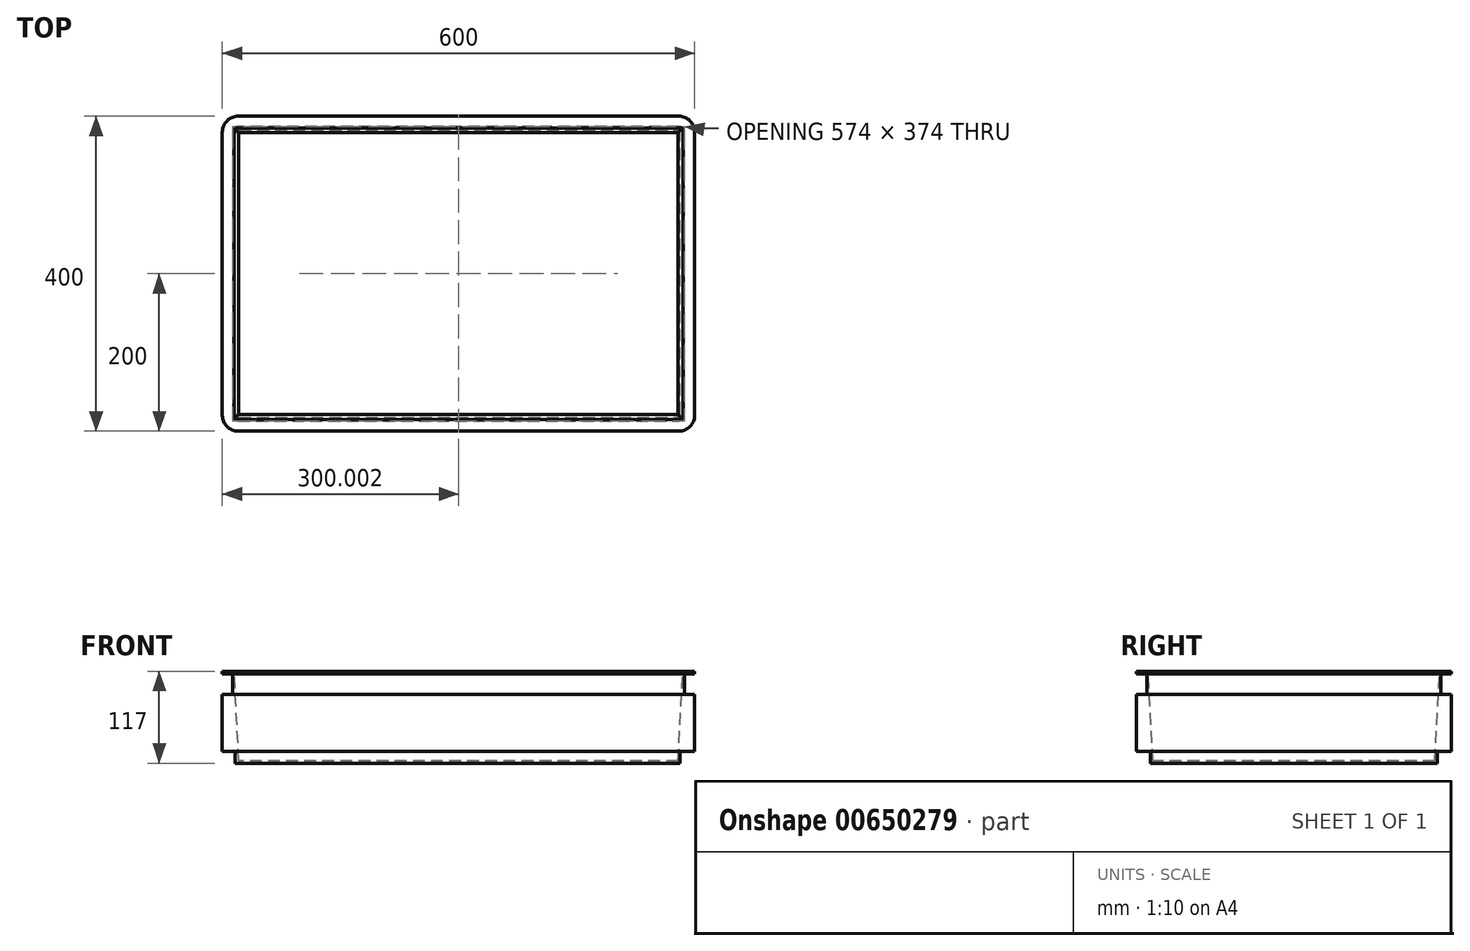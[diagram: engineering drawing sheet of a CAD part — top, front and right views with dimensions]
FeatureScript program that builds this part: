
annotation { "Feature Type Name" : "Feature", "Feature Type Description" : "" }
export const myFeature = defineFeature(function(context is Context, id is Id, definition is map)
    precondition{}
    {
        {
            var Q0;
            Q0=qCreatedBy(makeId("Top.planeOp"),FACE);
            var sketch = newSketch(context, id + "F0", { "sketchPlane" : qUnion([Q0])});
            skLineSegment(sketch, "E0.bottom", {"start": v(-291.39, 200) * mm, "end": v(308.61, 200) * mm});
            skLineSegment(sketch, "E0.top", {"start": v(-291.39, -200) * mm, "end": v(308.61, -200) * mm});
            skLineSegment(sketch, "E0.left", {"start": v(-291.39, 200) * mm, "end": v(-291.39, -200) * mm});
            skLineSegment(sketch, "E0.right", {"start": v(308.61, 200) * mm, "end": v(308.61, -200) * mm});
            skPoint(sketch, "E0.middle", {"position": v(8.61, 0) * mm});
            skSolve(sketch);
        }
        {
            var Q0;
            Q0=makeQuery(id+"F0.imprint","IMPRINT",FACE,{"disambiguationData":[TD([[makeQuery(id+"F0.imprint","IMPRINT",EDGE,{"derivedFrom":sQuery(id+"F0.wireOp",EDGE,"E0.bottom")}),-1.0]])]});
            extrude(context, id + "F1", {"entities" : qUnion([Q0]), "depth" : 117 * mm, "offsetDistance" : 25 * mm});
        }
        {
            var Q0;
            Q0=makeQuery(id+"F1.opExtrude","SWEPT_EDGE",EDGE,{"disambiguationData":[OSD([sQuery(id+"F0.wireOp",EDGE,"E0.top"),sQuery(id+"F0.wireOp",EDGE,"E0.left")])]});
            var Q1;
            Q1=makeQuery(id+"F1.opExtrude","SWEPT_EDGE",EDGE,{"disambiguationData":[OSD([sQuery(id+"F0.wireOp",EDGE,"E0.top"),sQuery(id+"F0.wireOp",EDGE,"E0.right")])]});
            var Q2;
            Q2=makeQuery(id+"F1.opExtrude","SWEPT_EDGE",EDGE,{"disambiguationData":[OSD([sQuery(id+"F0.wireOp",EDGE,"E0.bottom"),sQuery(id+"F0.wireOp",EDGE,"E0.right")])]});
            var Q3;
            Q3=makeQuery(id+"F1.opExtrude","SWEPT_EDGE",EDGE,{"disambiguationData":[OSD([sQuery(id+"F0.wireOp",EDGE,"E0.bottom"),sQuery(id+"F0.wireOp",EDGE,"E0.left")])]});
            fillet(context, id + "F2", {"entities" : qUnion([Q0, Q1, Q2, Q3]), "radius" : 20 * mm, "tangentPropagation" : true, "allowEdgeOverflow" : false});
        }
        {
            var Q0;
            Q0=makeQuery(id+"F1.opExtrude","CAP_FACE",FACE,{"disambiguationData":[OSD([sQuery(id+"F0.wireOp",EDGE,"E0.bottom"),sQuery(id+"F0.wireOp",EDGE,"E0.top"),sQuery(id+"F0.wireOp",EDGE,"E0.left"),sQuery(id+"F0.wireOp",EDGE,"E0.right")])],"isStart":true});
            var sketch = newSketch(context, id + "F3", { "sketchPlane" : qUnion([Q0])});
            skLineSegment(sketch, "E1.bottom", {"start": v(-270.1, 182.5) * mm, "end": v(284.9, 182.5) * mm});
            skLineSegment(sketch, "E1.top", {"start": v(-270.1, -182.5) * mm, "end": v(284.9, -182.5) * mm});
            skLineSegment(sketch, "E1.left", {"start": v(-275.1, 177.5) * mm, "end": v(-275.1, -177.5) * mm});
            skLineSegment(sketch, "E1.right", {"start": v(289.9, 177.5) * mm, "end": v(289.9, -177.5) * mm});
            skPoint(sketch, "E1.middle", {"position": v(7.4, 0) * mm});
            skLineSegment(sketch, "E2.0.0", {"start": v(288.61, 200) * mm, "end": v(-271.39, 200) * mm});
            skArc(sketch, "E2.0.1", {"start": v(-271.39, 200) * mm, "mid": v(-285.53, 194.14) * mm, "end": v(-291.39, 180) * mm});
            skLineSegment(sketch, "E2.0.2", {"start": v(-291.39, 180) * mm, "end": v(-291.39, -180) * mm});
            skArc(sketch, "E2.0.3", {"start": v(-291.39, -180) * mm, "mid": v(-285.53, -194.14) * mm, "end": v(-271.39, -200) * mm});
            skLineSegment(sketch, "E2.0.4", {"start": v(-271.39, -200) * mm, "end": v(288.61, -200) * mm});
            skArc(sketch, "E2.0.5", {"start": v(288.61, -200) * mm, "mid": v(302.75, -194.14) * mm, "end": v(308.61, -180) * mm});
            skLineSegment(sketch, "E2.0.6", {"start": v(308.61, -180) * mm, "end": v(308.61, 180) * mm});
            skArc(sketch, "E2.0.7", {"start": v(308.61, 180) * mm, "mid": v(302.75, 194.14) * mm, "end": v(288.61, 200) * mm});
            skPoint(sketch, "E3.visualSharp", {"position": v(-275.1, 182.5) * mm});
            skArc(sketch, "E3.filletArc", {"start": v(-270.1, 182.5) * mm, "mid": v(-273.63, 181.04) * mm, "end": v(-275.1, 177.5) * mm});
            skPoint(sketch, "E4.visualSharp", {"position": v(289.9, 182.5) * mm});
            skArc(sketch, "E4.filletArc", {"start": v(289.9, 177.5) * mm, "mid": v(288.44, 181.04) * mm, "end": v(284.9, 182.5) * mm});
            skPoint(sketch, "E5.visualSharp", {"position": v(289.9, -182.5) * mm});
            skArc(sketch, "E5.filletArc", {"start": v(284.9, -182.5) * mm, "mid": v(288.44, -181.04) * mm, "end": v(289.9, -177.5) * mm});
            skPoint(sketch, "E6.visualSharp", {"position": v(-275.1, -182.5) * mm});
            skArc(sketch, "E6.filletArc", {"start": v(-275.1, -177.5) * mm, "mid": v(-273.63, -181.04) * mm, "end": v(-270.1, -182.5) * mm});
            skSolve(sketch);
        }
        {
            var Q0;
            Q0=makeQuery(id+"F3.imprint","IMPRINT",FACE,{"disambiguationData":[TD([[makeQuery(id+"F3.imprint","IMPRINT",EDGE,{"derivedFrom":sQuery(id+"F3.wireOp",EDGE,"E1.bottom")}),1.0]])]});
            extrude(context, id + "F4", {"entities" : qUnion([Q0]), "operationType" : NewBodyOperationType.REMOVE, "oppositeDirection" : true, "depth" : 15 * mm, "offsetDistance" : 25 * mm});
        }
        {
            var Q0;
            Q0=makeQuery(id+"F1.opExtrude","CAP_FACE",FACE,{"disambiguationData":[OSD([sQuery(id+"F0.wireOp",EDGE,"E0.bottom"),sQuery(id+"F0.wireOp",EDGE,"E0.top"),sQuery(id+"F0.wireOp",EDGE,"E0.left"),sQuery(id+"F0.wireOp",EDGE,"E0.right")])],"isStart":false});
            cPlane(context, id + "F5", {"entities" : qUnion([Q0]), "cplaneType" : CPlaneType.OFFSET, "offset" : 3.5 * mm, "oppositeDirection" : true, "width" : 150 * mm, "height" : 150 * mm});
        }
        {
            var Q0;
            Q0=qCreatedBy(id+"F5.planeOp",FACE);
            var sketch = newSketch(context, id + "F6", { "sketchPlane" : qUnion([Q0])});
            skLineSegment(sketch, "E7.0.0", {"start": v(-291.39, 180) * mm, "end": v(-291.39, -180) * mm});
            skArc(sketch, "E7.0.1", {"start": v(-291.39, -180) * mm, "mid": v(-285.53, -194.14) * mm, "end": v(-271.39, -200) * mm});
            skLineSegment(sketch, "E7.0.2", {"start": v(-271.39, -200) * mm, "end": v(288.61, -200) * mm});
            skArc(sketch, "E7.0.3", {"start": v(288.61, -200) * mm, "mid": v(302.75, -194.14) * mm, "end": v(308.61, -180) * mm});
            skLineSegment(sketch, "E7.0.4", {"start": v(308.61, -180) * mm, "end": v(308.61, 180) * mm});
            skArc(sketch, "E7.0.5", {"start": v(308.61, 180) * mm, "mid": v(302.75, 194.14) * mm, "end": v(288.61, 200) * mm});
            skLineSegment(sketch, "E7.0.6", {"start": v(288.61, 200) * mm, "end": v(-271.39, 200) * mm});
            skArc(sketch, "E7.0.7", {"start": v(-271.39, 200) * mm, "mid": v(-285.53, 194.14) * mm, "end": v(-291.39, 180) * mm});
            skArc(sketch, "E8.0", {"start": v(-271.39, 187) * mm, "mid": v(-276.34, 184.95) * mm, "end": v(-278.39, 180) * mm});
            skLineSegment(sketch, "E8.1", {"start": v(288.61, 187) * mm, "end": v(-271.39, 187) * mm});
            skLineSegment(sketch, "E8.2", {"start": v(-278.39, 180) * mm, "end": v(-278.39, -180) * mm});
            skArc(sketch, "E8.3", {"start": v(295.61, 180) * mm, "mid": v(293.56, 184.95) * mm, "end": v(288.61, 187) * mm});
            skArc(sketch, "E8.4", {"start": v(-278.39, -180) * mm, "mid": v(-276.34, -184.95) * mm, "end": v(-271.39, -187) * mm});
            skLineSegment(sketch, "E8.5", {"start": v(-271.39, -187) * mm, "end": v(288.61, -187) * mm});
            skArc(sketch, "E8.6", {"start": v(288.61, -187) * mm, "mid": v(293.56, -184.95) * mm, "end": v(295.61, -180) * mm});
            skLineSegment(sketch, "E8.7", {"start": v(295.61, -180) * mm, "end": v(295.61, 180) * mm});
            skSolve(sketch);
        }
        {
            var Q0;
            Q0 = qSketchRegion(id + "F6", true);
            extrude(context, id + "F7", {"entities" : qUnion([Q0]), "operationType" : NewBodyOperationType.REMOVE, "oppositeDirection" : true, "depth" : 26 * mm, "offsetDistance" : 25 * mm});
        }
        {
            var Q0;
            Q0=makeQuery(id+"F1.opExtrude","CAP_FACE",FACE,{"disambiguationData":[OSD([sQuery(id+"F0.wireOp",EDGE,"E0.bottom"),sQuery(id+"F0.wireOp",EDGE,"E0.top"),sQuery(id+"F0.wireOp",EDGE,"E0.left"),sQuery(id+"F0.wireOp",EDGE,"E0.right")])],"isStart":false});
            var sketch = newSketch(context, id + "F8", { "sketchPlane" : qUnion([Q0])});
            skLineSegment(sketch, "E9.0", {"start": v(-276.39, 185) * mm, "end": v(-276.39, -185) * mm});
            skLineSegment(sketch, "E9.1", {"start": v(293.61, 185) * mm, "end": v(-276.39, 185) * mm});
            skLineSegment(sketch, "E9.2", {"start": v(293.61, -185) * mm, "end": v(293.61, 185) * mm});
            skLineSegment(sketch, "E9.3", {"start": v(-276.39, -185) * mm, "end": v(293.61, -185) * mm});
            skSolve(sketch);
        }
        {
            var Q0;
            Q0=makeQuery(id+"F8.imprint","IMPRINT",FACE,{"disambiguationData":[TD([[makeQuery(id+"F8.imprint","IMPRINT",EDGE,{"derivedFrom":sQuery(id+"F8.wireOp",EDGE,"E9.0")}),1.0]])]});
            extrude(context, id + "F9", {"entities" : qUnion([Q0]), "operationType" : NewBodyOperationType.REMOVE, "oppositeDirection" : true, "depth" : 114 * mm, "offsetDistance" : 25 * mm, "hasDraft" : true, "draftAngle" : 3 * degree, "draftPullDirection" : true});
        }
    });
